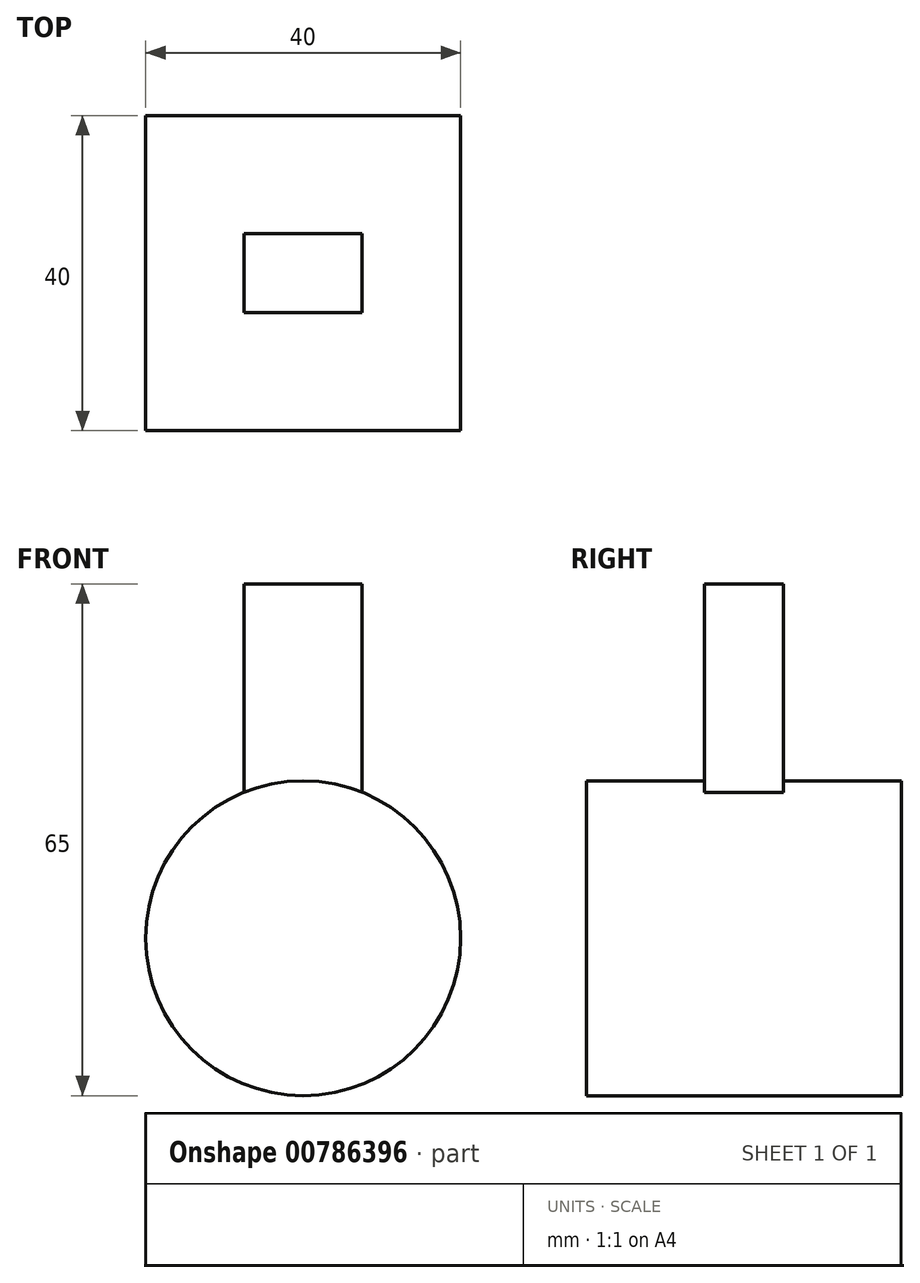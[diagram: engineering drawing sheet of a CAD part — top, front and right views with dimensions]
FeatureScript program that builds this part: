
annotation { "Feature Type Name" : "Feature", "Feature Type Description" : "" }
export const myFeature = defineFeature(function(context is Context, id is Id, definition is map)
    precondition{}
    {
        {
            var Q0;
            Q0=qCreatedBy(makeId("Front.planeOp"),FACE);
            var sketch = newSketch(context, id + "F0", { "sketchPlane" : qUnion([Q0])});
            skCircle(sketch, "E0", {"center": v(0, 0) * mm, "radius": 20 * mm});
            skSolve(sketch);
        }
        {
            var Q0;
            Q0 = qSketchRegion(id + "F0", true);
            extrude(context, id + "F1", {"entities" : qUnion([Q0]), "endBound" : BoundingType.SYMMETRIC, "depth" : 40 * mm, "offsetDistance" : 25 * mm});
        }
        {
            var Q0;
            Q0=qCreatedBy(makeId("Top.planeOp"),FACE);
            cPlane(context, id + "F2", {"entities" : qUnion([Q0]), "cplaneType" : CPlaneType.OFFSET, "offset" : 15 * mm, "width" : 150 * mm, "height" : 150 * mm});
        }
        {
            var Q0;
            Q0=qCreatedBy(id+"F2.planeOp",FACE);
            var sketch = newSketch(context, id + "F3", { "sketchPlane" : qUnion([Q0])});
            skLineSegment(sketch, "E1.bottom", {"start": v(7.5, -5) * mm, "end": v(-7.5, -5) * mm});
            skLineSegment(sketch, "E1.top", {"start": v(7.5, 5) * mm, "end": v(-7.5, 5) * mm});
            skLineSegment(sketch, "E1.left", {"start": v(7.5, -5) * mm, "end": v(7.5, 5) * mm});
            skLineSegment(sketch, "E1.right", {"start": v(-7.5, -5) * mm, "end": v(-7.5, 5) * mm});
            skPoint(sketch, "E1.middle", {"position": v(0, 0) * mm});
            skSolve(sketch);
        }
        {
            var Q0;
            Q0 = qSketchRegion(id + "F3", true);
            extrude(context, id + "F4", {"entities" : qUnion([Q0]), "operationType" : NewBodyOperationType.ADD, "depth" : 30 * mm, "offsetDistance" : 25 * mm});
        }
        {
            var Q0;
            Q0=qCreatedBy(makeId("Top.planeOp"),FACE);
            var sketch = newSketch(context, id + "F5", { "sketchPlane" : qUnion([Q0])});
            skLineSegment(sketch, "E2", {"start": v(0, 47.63) * mm, "end": v(0, -35.84) * mm});
            skSolve(sketch);
        }
    });
